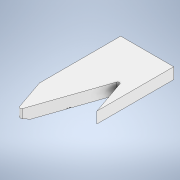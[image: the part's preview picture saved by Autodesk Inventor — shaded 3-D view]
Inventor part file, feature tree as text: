
AUTODESK INVENTOR PART (.ipt)
format: ipt  version: 2021.2 (Build 252289000, 289)  size: 319,488 bytes
history: native  units: in
note: dims shown in document units (in); Inventor stores cm internally (conversion verified against a paired STEP export)
features: sketch x4, extrude x3, hole x1, pattern_linear x1, plane x1, mirror x1
ambient origin geometry x8: Origin, YZ Plane, XZ Plane, XY Plane, X Axis, Y Axis, Z Axis, Center Point
bodies: Solid1 (feature_tree)
feature tree (11):
  extrude  "Extrusion1"  Depth=4.0in
  hole  "Hole2"  [1 undecoded]
  pattern_linear  "Rectangular Pattern1"  Spacing1=0.45in  [1 undecoded]
  extrude  "ExtrusionForText"  Depth=0.125in
  plane  "Work Plane1"
  mirror  "MirrorHoles"
  extrude  "Extrusion3"  Depth=0.125in TaperAngle=0.0deg
  sketch  "Sketch2"  dims[d0=6.0in d1=4.0in]
  sketch  "Sketch3"  dims[d2=0.8189in d4=1.135in]
  sketch  "SketchForText"  dims[d5=0.765in]
  sketch  "SketchForSplittingPart"  dims[d6=11.25in d7=0.0in d8=0.45in d16=0.13in d17=0.6in d18=0.563in d19=0.155in d20=0.5635in d21=0.625in d22=0.8108in d23=3.1496in d25=0.25in d26=0.05in d27=0.0in d30=0.125in d31=0.125in d32=-2.0in d33=0.0in d34=0.0in]
note: 2 required parameter values undecoded (feature->parameter linkage not recoverable at this tier; creation-order binding heuristic only, values carry confidence <= 0.55)
